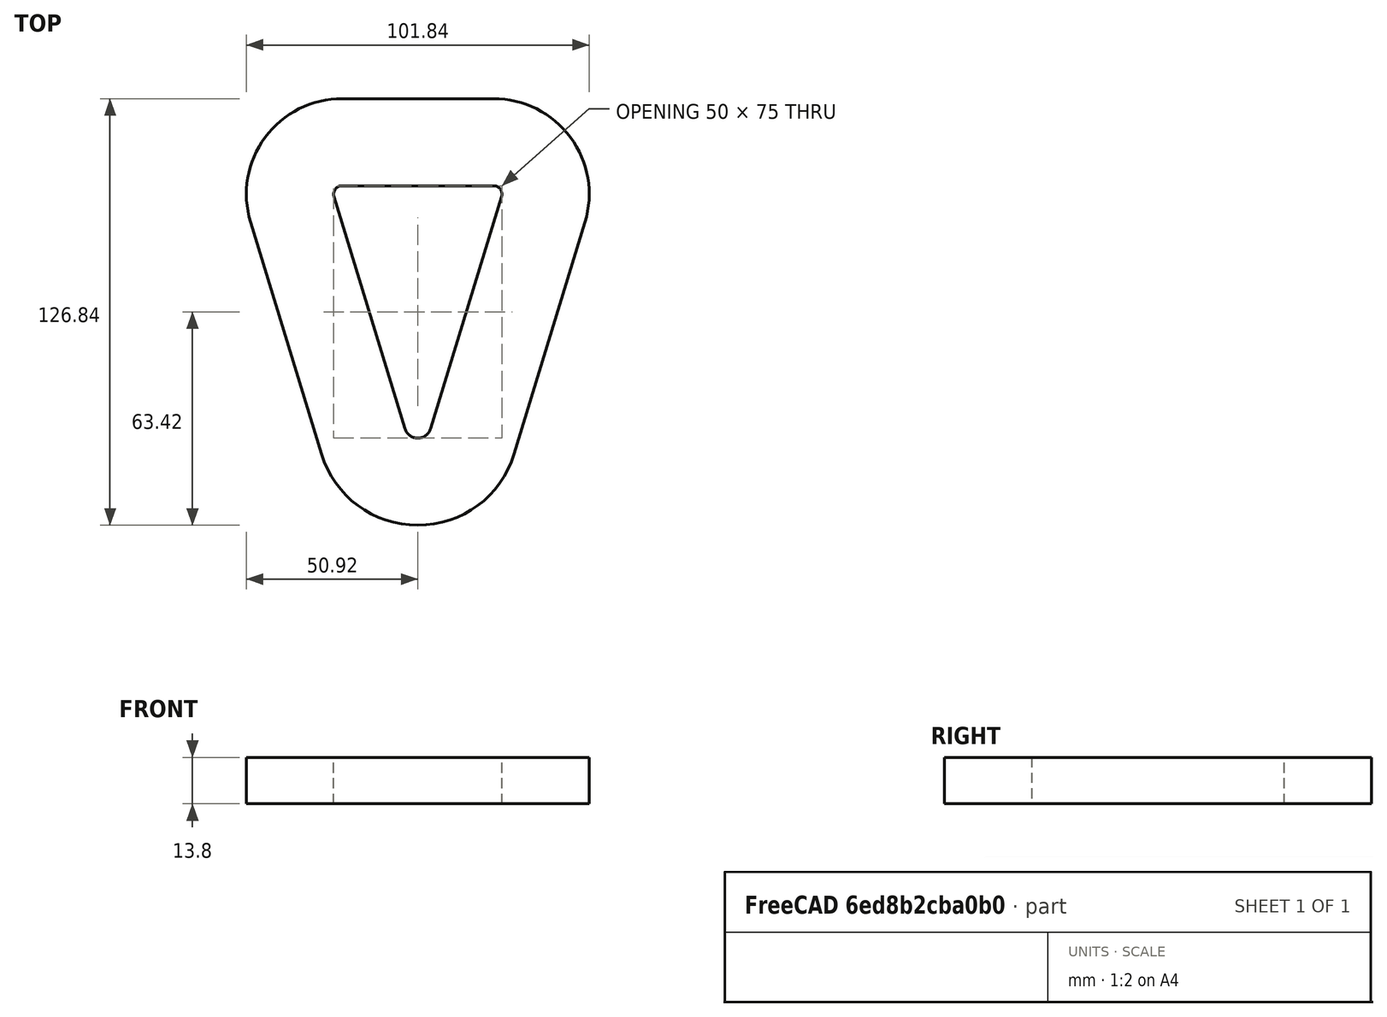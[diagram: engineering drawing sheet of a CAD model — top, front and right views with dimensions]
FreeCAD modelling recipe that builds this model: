
FCSTD DOCUMENT  (FreeCAD 0.21R33771 (Git))
Label: Stator_Coil_Triangular
License: All rights reserved
LicenseURL: http://en.wikipedia.org/wiki/All_rights_reserved
objects: Sketcher::SketchObject×1, PartDesign::Pad×1, PartDesign::Body×1, Spreadsheet::Sheet×1
note: 4 computed .brp shape members not serialized (recipe doc carries the construction recipe); baked Part::Feature solids carry a one-line shape summary decoded from their .brp
EXTERNAL_REF file=../../Master_of_Puppets.FCStd obj=Alternator
EXTERNAL_REF file=../../Master_of_Puppets.FCStd obj=Spreadsheet

FEATURE [Sketcher::SketchObject] Sketch
  FullyConstrained = true
  MapMode = 5
  Support = -> [XY_Plane]
  expr: Constraints[0] = Spreadsheet.CoilWinderPinRadius
  expr: Constraints[15] = Spreadsheet.CoilLegWidth
  expr: Constraints[25] = Spreadsheet.MagnetWidth
  expr: Constraints[29] = Spreadsheet.MagnetLength
  expr: Constraints[2] = Spreadsheet.InnerBottomArcRadius
  sketch-geometry (18):
    g0: Circle CenterX=-22.5 CenterY=72.5 CenterZ=0 NormalX=0 NormalY=0 NormalZ=1 AngleXU=0 Radius=2.5
    g1: Circle CenterX=22.5 CenterY=72.5 CenterZ=0 NormalX=0 NormalY=0 NormalZ=1 AngleXU=0 Radius=2.5
    g2: Circle CenterX=0 CenterY=4 CenterZ=0 NormalX=0 NormalY=0 NormalZ=1 AngleXU=0 Radius=4
    g3: LineSegment StartX=3.82539 StartY=2.83108 StartZ=0 EndX=24.8909 EndY=71.7694 EndZ=0
    g4: LineSegment StartX=-22.5 StartY=75 StartZ=0 EndX=22.5 EndY=75 EndZ=0
    g5: LineSegment StartX=-3.82539 StartY=2.83108 StartZ=0 EndX=-24.8909 EndY=71.7694 EndZ=0
    g6: ArcOfCircle CenterX=0 CenterY=4 CenterZ=0 NormalX=0 NormalY=0 NormalZ=1 AngleXU=0 Radius=4 StartAngle=3.43815 EndAngle=5.98663
    g7: LineSegment StartX=-22.5 StartY=100.92 StartZ=0 EndX=22.5 EndY=100.92 EndZ=0
    g8: LineSegment StartX=-49.6794 StartY=64.1948 StartZ=0 EndX=-28.6139 EndY=-4.74355 EndZ=0
    g9: LineSegment StartX=49.6794 StartY=64.1948 StartZ=0 EndX=28.6139 EndY=-4.74355 EndZ=0
    g10: ArcOfCircle CenterX=-22.5 CenterY=72.5 CenterZ=0 NormalX=0 NormalY=0 NormalZ=1 AngleXU=0 Radius=28.42 StartAngle=1.5708 EndAngle=3.43815
    g11: ArcOfCircle CenterX=22.5 CenterY=72.5 CenterZ=0 NormalX=0 NormalY=0 NormalZ=1 AngleXU=0 Radius=28.42 StartAngle=5.98663 EndAngle=7.85398
    g12: ArcOfCircle CenterX=0 CenterY=4 CenterZ=0 NormalX=0 NormalY=0 NormalZ=1 AngleXU=0 Radius=29.92 StartAngle=3.43815 EndAngle=5.98663
    g13: ArcOfCircle CenterX=-22.5 CenterY=72.5 CenterZ=0 NormalX=0 NormalY=0 NormalZ=1 AngleXU=0 Radius=2.5 StartAngle=1.5708 EndAngle=3.14159
    g14: ArcOfCircle CenterX=-22.5 CenterY=72.5 CenterZ=0 NormalX=0 NormalY=0 NormalZ=1 AngleXU=0 Radius=2.5 StartAngle=3.14159 EndAngle=3.43815
    g15: ArcOfCircle CenterX=22.5 CenterY=72.5 CenterZ=0 NormalX=0 NormalY=0 NormalZ=1 AngleXU=0 Radius=2.5 StartAngle=5.98663 EndAngle=6.28319
    g16: ArcOfCircle CenterX=22.5 CenterY=72.5 CenterZ=0 NormalX=0 NormalY=0 NormalZ=1 AngleXU=0 Radius=2.5 StartAngle=9e-16 EndAngle=1.5708
    g17: GeomPoint X=-22.5 Y=75 Z=0
  constraints (39):
    c: Radius(g0) = 2.5
    c: Equal(g1,g0)
    c: Radius(g2) = 4
    c: Tangent(g3,g1) = -1.5708
    c: Tangent(g5,g0) = 1.5708
    c: Coincident(g6,g2)
    c: Horizontal(g4)
    c: Equal(g6,g2)
    c: Tangent(g6,g5) = 1.5708
    c: Tangent(g3,g6) = -1.5708
    c: Tangent(g4,g0) = 1.5708
    c: Horizontal(g7)
    c: Parallel(g9,g3)
    c: Tangent(g12,g9) = 1.5708
    c: Tangent(g12,g8) = -1.5708
    c: DistanceY(g4,g7) = 25.92
    c: Tangent(g10,g7) = 1.5708
    c: Tangent(g10,g8) = -1.5708
    c: Tangent(g11,g9) = 1.5708
    c: Tangent(g11,g7) = 1.5708
    c: Coincident(g13,g10)
    c: Coincident(g13,g4)
    c: Coincident(g14,g5)
    c: Coincident(g15,g11)
    c: Coincident(g15,g3)
    c: DistanceX(g13,g15) = 50
    c: Horizontal(g15,g13)
    c: Tangent(g14,g13) = -1.5708
    c: Coincident(g14,g0)
    c: Distance(g-1,g4) = 75
    c: Coincident(g6,g12)
    c: PointOnObject(g6,g-2)
    c: Tangent(g16,g15) = -1.5708
    c: Coincident(g1,g11)
    c: Tangent(g16,g4) = 1.5708
    c: Horizontal(g15,g11)
    c: Coincident(g17,g4)
    c: Symmetric(g10,g11,g-2)
    c: PointOnObject(g-1,g6)
FEATURE [PartDesign::Pad] Pad
  AllowMultiFace = false
  Direction = (0,0,1)
  Length = 13.8
  Length2 = 100
  Profile = -> Sketch
  Type = 0
  expr: Length = Spreadsheet.CoilThickness
FEATURE [PartDesign::Body] Body  label="Stator_Coil"
  Group = -> [Sketch,Pad]
  Origin = -> Origin
  Tip = -> Pad
FEATURE [Spreadsheet::Sheet] Spreadsheet
  cells = A1='Inputs; A2='CoilLegWidth; B2(CoilLegWidth)==Master_of_Puppets#Spreadsheet.CoilLegWidth; A3='CoilHoleWidthAtOuterRadius; B3(CoilHoleWidthAtOuterRadius)==Master_of_Puppets#Spreadsheet.CoilHoleWidthAtOuterRadius; A4='CoilHoleWidthAtInnerRadius; B4(CoilHoleWidthAtInnerRadius)==Master_of_Puppets#Spreadsheet.CoilHoleWidthAtInnerRadius; A5='MagnetWidth; B5(MagnetWidth)==Master_of_Puppets#Spreadsheet.MagnetWidth; A6='CoilWinderPinRadius; B6(CoilWinderPinRadius)==Master_of_Puppets#Alternator.CoilWinderPinRadius; A7='CoilThickness; B7(CoilThickness)==Master_of_Puppets#Alternator.CoilThickness; A8='MagnetLength; B8(MagnetLength)==Master_of_Puppets#Alternator.MagnetLength; A9='CoilType; B9(CoilType)==Master_of_Puppets#Alternator.CoilType; A10='Calculated; A11='InnerBottomArcRadius; B11(InnerBottomArcRadius)==CoilType == 3 ? CoilHoleWidthAtInnerRadius / 2 : 4; C11='Duplicated in Stator_Coil_Triangular_Reduced
